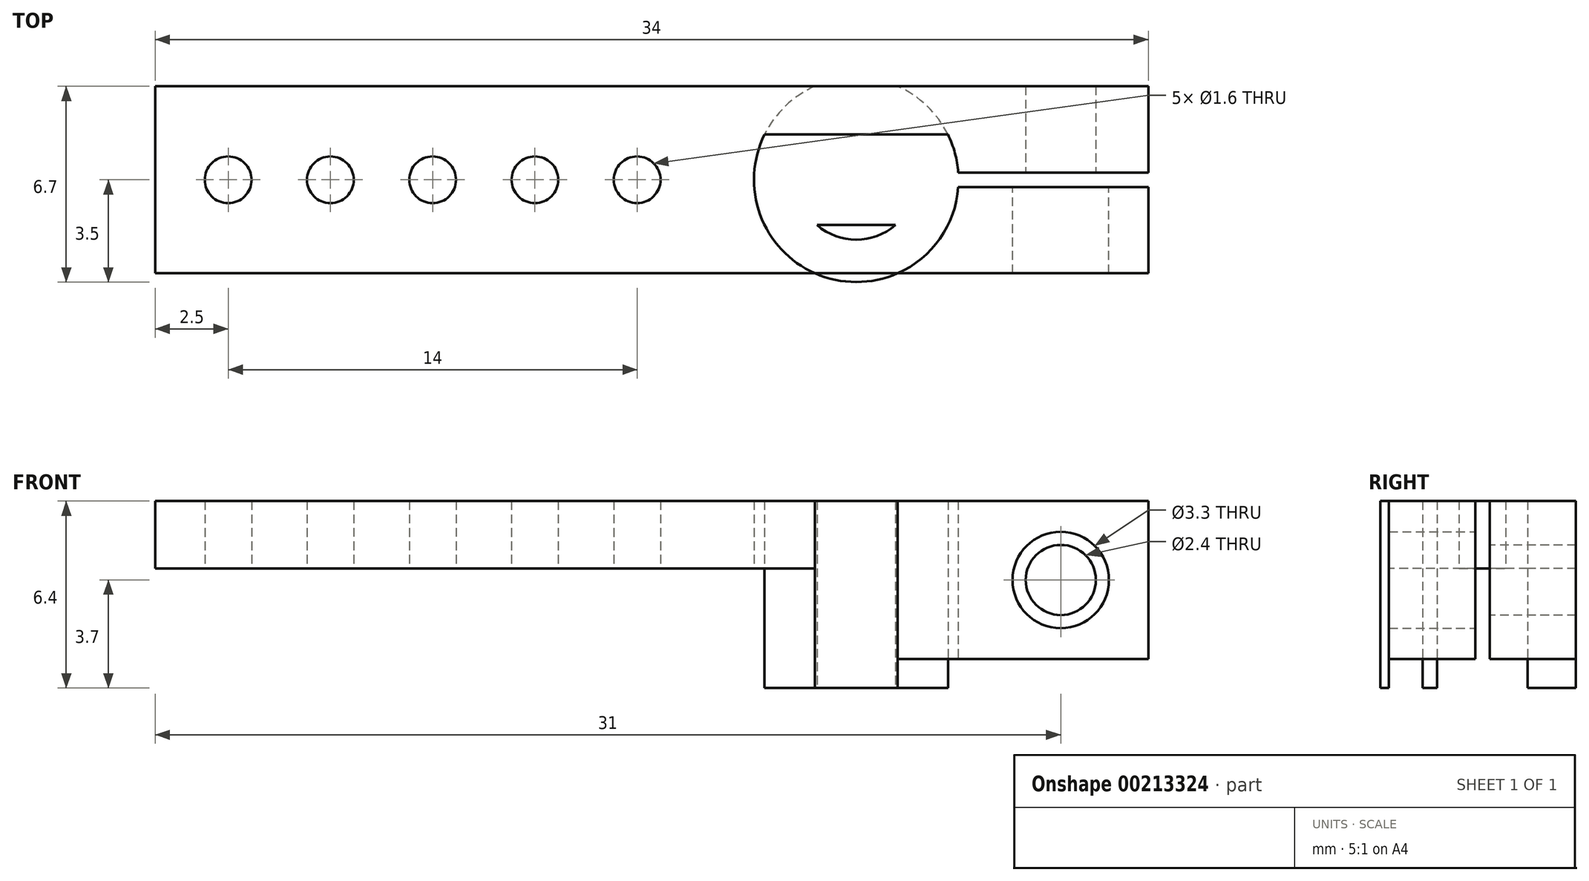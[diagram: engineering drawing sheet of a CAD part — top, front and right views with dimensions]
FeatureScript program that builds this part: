
annotation { "Feature Type Name" : "Feature", "Feature Type Description" : "" }
export const myFeature = defineFeature(function(context is Context, id is Id, definition is map)
    precondition{}
    {
        {
            var Q0;
            Q0=qCreatedBy(makeId("Top.planeOp"),FACE);
            var sketch = newSketch(context, id + "F0", { "sketchPlane" : qUnion([Q0])});
            skLineSegment(sketch, "E0.bottom", {"start": v(5.54, -1.55) * mm, "end": v(-5.54, -1.55) * mm});
            skLineSegment(sketch, "E0.top", {"start": v(5.54, 1.55) * mm, "end": v(-5.54, 1.55) * mm});
            skPoint(sketch, "E0.middle", {"position": v(0, 0) * mm});
            skCircle(sketch, "E1", {"center": v(0, 0) * mm, "radius": 3.5 * mm});
            skArc(sketch, "E2", {"start": v(1.34, -1.55) * mm, "mid": v(-1.55, -1.34) * mm, "end": v(-1.34, 1.55) * mm});
            skCircle(sketch, "E3", {"center": v(0, 0) * mm, "radius": 2.05 * mm});
            skLineSegment(sketch, "E4.bottom", {"start": v(10, 3.2) * mm, "end": v(-24, 3.2) * mm});
            skLineSegment(sketch, "E4.top", {"start": v(10, -3.2) * mm, "end": v(-24, -3.2) * mm});
            skLineSegment(sketch, "E4.left", {"start": v(10, 3.2) * mm, "end": v(10, -3.2) * mm});
            skLineSegment(sketch, "E4.right", {"start": v(-24, 3.2) * mm, "end": v(-24, -3.2) * mm});
            skPoint(sketch, "E4.middle", {"position": v(-7, 0) * mm});
            skCircle(sketch, "E5", {"center": v(-21.5, 0) * mm, "radius": 0.8 * mm});
            skCircle(sketch, "E6", {"center": v(-18, 0) * mm, "radius": 0.8 * mm});
            skCircle(sketch, "E7", {"center": v(-14.5, 0) * mm, "radius": 0.8 * mm});
            skCircle(sketch, "E8", {"center": v(-11, 0) * mm, "radius": 0.8 * mm});
            skCircle(sketch, "E9", {"center": v(-7.5, 0) * mm, "radius": 0.8 * mm});
            skPoint(sketch, "E10", {"position": v(-1.34, -1.55) * mm});
            skSolve(sketch);
        }
        {
            var Q0;
            {var subQ0=sQuery(id+"F0.wireOp",EDGE,"E4.right");Q0=makeQuery(id+"F0.imprint","IMPRINT",FACE,{"disambiguationData":[TD([[makeQuery(id+"F0.imprint","IMPRINT",EDGE,{"derivedFrom":subQ0}),1.0]])]});}
            var Q1;
            {var subQ0=sQuery(id+"F0.wireOp",EDGE,"E1");var subQ1=sQuery(id+"F0.wireOp",EDGE,"E0.bottom");var subQ2=makeQuery(id+"F0.imprint","INTERSECT",VERTEX,{"disambiguationData":[OD(1.0)],"derivedFrom":[subQ1,subQ0]});Q1=makeQuery(id+"F0.imprint","IMPRINT",FACE,{"disambiguationData":[TD([[makeQuery(id+"F0.imprint","IMPRINT",EDGE,{"disambiguationData":[TD([[subQ2,1.0]])],"derivedFrom":subQ1}),-1.0]])]});}
            var Q2;
            {var subQ0=sQuery(id+"F0.wireOp",EDGE,"E1");var subQ1=sQuery(id+"F0.wireOp",EDGE,"E0.bottom");var subQ2=makeQuery(id+"F0.imprint","INTERSECT",VERTEX,{"disambiguationData":[OD(0.0)],"derivedFrom":[subQ1,subQ0]});Q2=makeQuery(id+"F0.imprint","IMPRINT",FACE,{"disambiguationData":[TD([[makeQuery(id+"F0.imprint","IMPRINT",EDGE,{"disambiguationData":[TD([[subQ2,-1.0]])],"derivedFrom":subQ1}),1.0]])]});}
            var Q3;
            {var subQ0=sQuery(id+"F0.wireOp",EDGE,"E1");var subQ1=sQuery(id+"F0.wireOp",EDGE,"E0.top");var subQ5=makeQuery(id+"F0.imprint","INTERSECT",VERTEX,{"disambiguationData":[OD(0.0)],"derivedFrom":[subQ1,subQ0]});Q3=makeQuery(id+"F0.imprint","IMPRINT",FACE,{"disambiguationData":[TD([[makeQuery(id+"F0.imprint","IMPRINT",EDGE,{"disambiguationData":[TD([[subQ5,-1.0]])],"derivedFrom":subQ1}),-1.0]])]});}
            var Q4;
            {var subQ0=sQuery(id+"F0.wireOp",EDGE,"E3");var subQ1=sQuery(id+"F0.wireOp",EDGE,"E0.top");var subQ2=makeQuery(id+"F0.imprint","INTERSECT",VERTEX,{"disambiguationData":[OD(0.0)],"derivedFrom":[subQ1,subQ0]});Q4=makeQuery(id+"F0.imprint","IMPRINT",FACE,{"disambiguationData":[TD([[makeQuery(id+"F0.imprint","IMPRINT",EDGE,{"disambiguationData":[TD([[subQ2,-1.0]])],"derivedFrom":subQ1}),-1.0]])]});}
            var Q5;
            {var subQ0=sQuery(id+"F0.wireOp",EDGE,"E3");var subQ1=sQuery(id+"F0.wireOp",EDGE,"E0.bottom");var subQ2=makeQuery(id+"F0.imprint","INTERSECT",VERTEX,{"disambiguationData":[OD(0.0)],"derivedFrom":[subQ1,subQ0]});Q5=makeQuery(id+"F0.imprint","IMPRINT",FACE,{"disambiguationData":[TD([[makeQuery(id+"F0.imprint","IMPRINT",EDGE,{"disambiguationData":[TD([[subQ2,-1.0]])],"derivedFrom":subQ1}),1.0]])]});}
            var Q6;
            {var subQ0=sQuery(id+"F0.wireOp",EDGE,"E1");var subQ1=sQuery(id+"F0.wireOp",EDGE,"E0.bottom");var subQ2=makeQuery(id+"F0.imprint","INTERSECT",VERTEX,{"disambiguationData":[OD(0.0)],"derivedFrom":[subQ1,subQ0]});Q6=makeQuery(id+"F0.imprint","IMPRINT",FACE,{"disambiguationData":[TD([[makeQuery(id+"F0.imprint","IMPRINT",EDGE,{"disambiguationData":[TD([[subQ2,-1.0]])],"derivedFrom":subQ1}),-1.0]])]});}
            var Q7;
            {var subQ0=sQuery(id+"F0.wireOp",EDGE,"E4.left");Q7=makeQuery(id+"F0.imprint","IMPRINT",FACE,{"disambiguationData":[TD([[makeQuery(id+"F0.imprint","IMPRINT",EDGE,{"derivedFrom":subQ0}),-1.0]])]});}
            var Q8;
            {var subQ0=sQuery(id+"F0.wireOp",EDGE,"E4.top");var subQ1=sQuery(id+"F0.wireOp",EDGE,"E1");var subQ2=makeQuery(id+"F0.imprint","INTERSECT",VERTEX,{"disambiguationData":[OD(0.0)],"derivedFrom":[subQ1,subQ0]});Q8=makeQuery(id+"F0.imprint","IMPRINT",FACE,{"disambiguationData":[TD([[makeQuery(id+"F0.imprint","IMPRINT",EDGE,{"disambiguationData":[TD([[subQ2,-1.0]])],"derivedFrom":subQ1}),1.0]])]});}
            var Q9;
            {var subQ0=sQuery(id+"F0.wireOp",EDGE,"E4.bottom");var subQ1=sQuery(id+"F0.wireOp",EDGE,"E1");var subQ2=makeQuery(id+"F0.imprint","INTERSECT",VERTEX,{"disambiguationData":[OD(0.0)],"derivedFrom":[subQ1,subQ0]});Q9=makeQuery(id+"F0.imprint","IMPRINT",FACE,{"disambiguationData":[TD([[makeQuery(id+"F0.imprint","IMPRINT",EDGE,{"disambiguationData":[TD([[subQ2,-1.0]])],"derivedFrom":subQ1}),1.0]])]});}
            extrude(context, id + "F1", {"entities" : qUnion([Q0, Q1, Q2, Q3, Q4, Q5, Q6, Q7, Q8, Q9]), "depth" : 6.4 * mm});
        }
        {
            var Q0;
            {var subQ0=sQuery(id+"F0.wireOp",EDGE,"E4.left");Q0=makeQuery(id+"F0.imprint","IMPRINT",FACE,{"disambiguationData":[TD([[makeQuery(id+"F0.imprint","IMPRINT",EDGE,{"derivedFrom":subQ0}),-1.0]])]});}
            extrude(context, id + "F2", {"entities" : qUnion([Q0]), "operationType" : NewBodyOperationType.REMOVE, "depth" : 1 * mm});
        }
        {
            var Q0;
            {var subQ0=sQuery(id+"F0.wireOp",EDGE,"E4.right");Q0=makeQuery(id+"F0.imprint","IMPRINT",FACE,{"disambiguationData":[TD([[makeQuery(id+"F0.imprint","IMPRINT",EDGE,{"derivedFrom":subQ0}),1.0]])]});}
            extrude(context, id + "F3", {"entities" : qUnion([Q0]), "operationType" : NewBodyOperationType.REMOVE, "depth" : 4.1 * mm});
        }
        {
            var Q0;
            Q0=qCreatedBy(makeId("Right.planeOp"),FACE);
            var sketch = newSketch(context, id + "F4", { "sketchPlane" : qUnion([Q0])});
            skLineSegment(sketch, "E11.bottom", {"start": v(-0.25, -7.5) * mm, "end": v(0.25, -7.5) * mm});
            skLineSegment(sketch, "E11.top", {"start": v(-0.25, 7.5) * mm, "end": v(0.25, 7.5) * mm});
            skLineSegment(sketch, "E11.left", {"start": v(-0.25, -7.5) * mm, "end": v(-0.25, 7.5) * mm});
            skLineSegment(sketch, "E11.right", {"start": v(0.25, -7.5) * mm, "end": v(0.25, 7.5) * mm});
            skPoint(sketch, "E11.middle", {"position": v(0, 0) * mm});
            skSolve(sketch);
        }
        {
            var Q0;
            Q0=qSketchRegion(id+"F4",true);
            extrude(context, id + "F5", {"entities" : qUnion([Q0]), "operationType" : NewBodyOperationType.REMOVE, "depth" : 25 * mm});
        }
        {
            var Q0;
            Q0=qCreatedBy(makeId("Front.planeOp"),FACE);
            var sketch = newSketch(context, id + "F6", { "sketchPlane" : qUnion([Q0])});
            skPoint(sketch, "E12", {"position": v(7, 3.7) * mm});
            skSolve(sketch);
        }
        {
            var Q0;
            Q0=sQuery(id+"F6.wireOp",VERTEX,"E12");
            var Q1;
            Q1=makeQuery(id+"F1.opExtrude","SWEPT_BODY",BODY,{"disambiguationData":[OSD([sQuery(id+"F0.wireOp",EDGE,"E0.bottom"),sQuery(id+"F0.wireOp",EDGE,"E0.top"),sQuery(id+"F0.wireOp",EDGE,"E1"),sQuery(id+"F0.wireOp",EDGE,"E3"),sQuery(id+"F0.wireOp",EDGE,"E4.bottom"),sQuery(id+"F0.wireOp",EDGE,"E4.top"),sQuery(id+"F0.wireOp",EDGE,"E4.left"),sQuery(id+"F0.wireOp",EDGE,"E4.right"),sQuery(id+"F0.wireOp",EDGE,"E5"),sQuery(id+"F0.wireOp",EDGE,"E6"),sQuery(id+"F0.wireOp",EDGE,"E7"),sQuery(id+"F0.wireOp",EDGE,"E8"),sQuery(id+"F0.wireOp",EDGE,"E9")])]});
            hole(context, id + "F7", {"style" : HoleStyle.SIMPLE, "endStyle" : HoleEndStyle.BLIND, "oppositeDirection" : true, "standardTappedOrClearance" : lookupTablePath({ "standard" : "ISO", "fit" : "Normal", "size" : "M3", "type" : "Clearance" }), "standardBlindInLast" : lookupTablePath({ "fit" : "Standard", "standard" : "ISO", "size" : "M3", "type" : "Clearance" }), "holeDiameter" : 3.3 * mm, "holeDepth" : 3.2 * mm, "startFromSketch" : true, "locations" : qUnion([Q0]), "scope" : qUnion([Q1])});
        }
        {
            var Q0;
            Q0=sQuery(id+"F6.wireOp",VERTEX,"E12");
            var Q1;
            Q1=makeQuery(id+"F1.opExtrude","SWEPT_BODY",BODY,{"disambiguationData":[OSD([sQuery(id+"F0.wireOp",EDGE,"E0.bottom"),sQuery(id+"F0.wireOp",EDGE,"E0.top"),sQuery(id+"F0.wireOp",EDGE,"E1"),sQuery(id+"F0.wireOp",EDGE,"E3"),sQuery(id+"F0.wireOp",EDGE,"E4.bottom"),sQuery(id+"F0.wireOp",EDGE,"E4.top"),sQuery(id+"F0.wireOp",EDGE,"E4.left"),sQuery(id+"F0.wireOp",EDGE,"E4.right"),sQuery(id+"F0.wireOp",EDGE,"E5"),sQuery(id+"F0.wireOp",EDGE,"E6"),sQuery(id+"F0.wireOp",EDGE,"E7"),sQuery(id+"F0.wireOp",EDGE,"E8"),sQuery(id+"F0.wireOp",EDGE,"E9")])]});
            hole(context, id + "F8", {"style" : HoleStyle.SIMPLE, "endStyle" : HoleEndStyle.BLIND, "standardTappedOrClearance" : lookupTablePath({ "standard" : "ISO", "engagement" : "75%", "pitch" : "0.6 mm", "size" : "M3", "type" : "Tapped" }), "standardBlindInLast" : lookupTablePath({ "standard" : "ISO", "engagement" : "75%", "pitch" : "0.6 mm", "size" : "M3", "type" : "Tapped" }), "holeDiameter" : 2.4 * mm, "holeDepth" : 3.5 * mm, "startFromSketch" : true, "locations" : qUnion([Q0]), "scope" : qUnion([Q1])});
        }
    });
